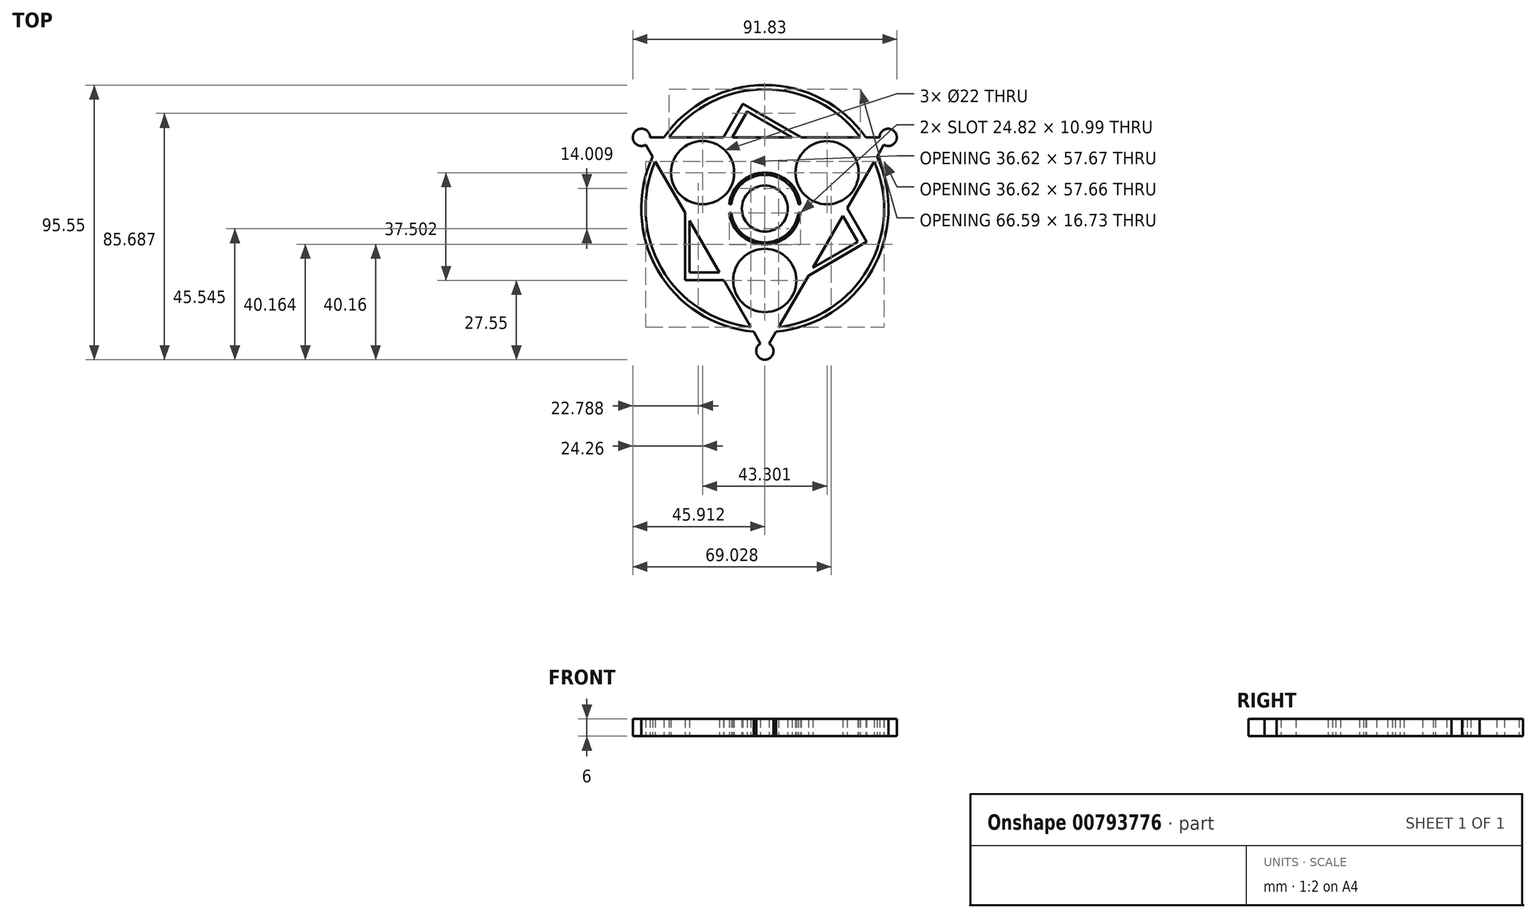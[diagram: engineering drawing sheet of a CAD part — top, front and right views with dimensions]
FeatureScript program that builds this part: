
annotation { "Feature Type Name" : "Feature", "Feature Type Description" : "" }
export const myFeature = defineFeature(function(context is Context, id is Id, definition is map)
    precondition{}
    {
        {
            var Q0;
            Q0=qCreatedBy(makeId("Top.planeOp"),FACE);
            var sketch = newSketch(context, id + "F0", { "sketchPlane" : qUnion([Q0])});
            skCircle(sketch, "E0", {"center": v(0, 0) * mm, "radius": 8 * mm});
            skLineSegment(sketch, "E1.0", {"start": v(41.42, 22.17) * mm, "end": v(39.03, 18.04) * mm});
            skLineSegment(sketch, "E1.1", {"start": v(-1.5, -46.95) * mm, "end": v(-3.89, -42.82) * mm});
            skLineSegment(sketch, "E1.2", {"start": v(-39.91, 24.78) * mm, "end": v(-35.14, 24.78) * mm});
            skPoint(sketch, "E1.0.midPoint", {"position": v(21.46, -12.39) * mm});
            skArc(sketch, "E2", {"start": v(3.88, -42.82) * mm, "mid": v(37.24, -21.5) * mm, "end": v(39.03, 18.04) * mm});
            skArc(sketch, "E3", {"start": v(4.8, -41.22) * mm, "mid": v(35.94, -20.75) * mm, "end": v(38.1, 16.44) * mm});
            skLineSegment(sketch, "E4.trimOffspring", {"start": v(3.88, -42.82) * mm, "end": v(1.5, -46.95) * mm});
            skLineSegment(sketch, "E5.trimOffspring", {"start": v(-4.81, -41.22) * mm, "end": v(-14.23, -24.9) * mm});
            skArc(sketch, "E6.trimOffspring", {"start": v(35.15, 24.77) * mm, "mid": v(0, 43) * mm, "end": v(-35.14, 24.78) * mm});
            skArc(sketch, "E7.trimOffspring", {"start": v(33.3, 24.77) * mm, "mid": v(0, 41.5) * mm, "end": v(-33.3, 24.78) * mm});
            skLineSegment(sketch, "E8.trimOffspring", {"start": v(35.15, 24.77) * mm, "end": v(39.92, 24.77) * mm});
            skLineSegment(sketch, "E9.trimOffspring", {"start": v(38.1, 16.44) * mm, "end": v(28.68, 0.12) * mm});
            skArc(sketch, "E10.trimOffspring", {"start": v(-39.03, 18.05) * mm, "mid": v(-37.24, -21.5) * mm, "end": v(-3.89, -42.82) * mm});
            skArc(sketch, "E11.trimOffspring", {"start": v(-38.1, 16.45) * mm, "mid": v(-35.94, -20.75) * mm, "end": v(-4.81, -41.22) * mm});
            skLineSegment(sketch, "E12.trimOffspring", {"start": v(-33.3, 24.78) * mm, "end": v(-14.45, 24.78) * mm});
            skLineSegment(sketch, "E13.trimOffspring", {"start": v(-39.03, 18.05) * mm, "end": v(-41.41, 22.18) * mm});
            skPoint(sketch, "E14.0.midPoint", {"position": v(-9.59, -5.4) * mm});
            skCircle(sketch, "E15", {"center": v(0, -25) * mm, "radius": 11 * mm});
            skCircle(sketch, "E16.1.0", {"center": v(21.65, 12.5) * mm, "radius": 11 * mm});
            skCircle(sketch, "E16.2.0", {"center": v(-21.65, 12.5) * mm, "radius": 11 * mm});
            skArc(sketch, "E17", {"start": v(11.65, 1.5) * mm, "mid": v(0, 11.75) * mm, "end": v(-11.65, 1.5) * mm});
            skArc(sketch, "E18", {"start": v(12.4, 1.5) * mm, "mid": v(0, 12.5) * mm, "end": v(-12.4, 1.5) * mm});
            skLineSegment(sketch, "E19", {"start": v(-12.4, 1.5) * mm, "end": v(-11.65, 1.5) * mm});
            skLineSegment(sketch, "E20.trimOffspring", {"start": v(11.65, 1.5) * mm, "end": v(12.4, 1.5) * mm});
            skArc(sketch, "E21.MirrorCS", {"start": v(11.65, -1.5) * mm, "mid": v(0, -11.75) * mm, "end": v(-11.65, -1.5) * mm});
            skArc(sketch, "E22.MirrorCS", {"start": v(12.4, -1.5) * mm, "mid": v(0, -12.5) * mm, "end": v(-12.4, -1.5) * mm});
            skArc(sketch, "E23", {"start": v(-1.5, -46.95) * mm, "mid": v(0, -52.55) * mm, "end": v(1.5, -46.95) * mm});
            skArc(sketch, "E24.1.0", {"start": v(41.42, 22.17) * mm, "mid": v(45.51, 26.27) * mm, "end": v(39.92, 24.77) * mm});
            skArc(sketch, "E24.2.0", {"start": v(-39.91, 24.78) * mm, "mid": v(-45.5, 26.28) * mm, "end": v(-41.41, 22.18) * mm});
            skLineSegment(sketch, "E25.top", {"start": v(-27.77, -24.9) * mm, "end": v(-14.23, -24.9) * mm});
            skLineSegment(sketch, "E25.left", {"start": v(-27.77, -1.44) * mm, "end": v(-27.77, -24.9) * mm});
            skLineSegment(sketch, "E26.top", {"start": v(-26.2, -22.25) * mm, "end": v(-15.77, -22.25) * mm});
            skLineSegment(sketch, "E26.left", {"start": v(-26.2, -4.17) * mm, "end": v(-26.2, -22.25) * mm});
            skLineSegment(sketch, "E27.trimOffspring", {"start": v(-27.77, -1.44) * mm, "end": v(-38.1, 16.45) * mm});
            skLineSegment(sketch, "E28.trimOffspring", {"start": v(-15.77, -22.25) * mm, "end": v(-26.2, -4.17) * mm});
            skLineSegment(sketch, "E29.1.0", {"start": v(15.14, -23.33) * mm, "end": v(35.45, -11.6) * mm});
            skLineSegment(sketch, "E29.1.1", {"start": v(35.45, -11.6) * mm, "end": v(28.68, 0.12) * mm});
            skLineSegment(sketch, "E29.1.2", {"start": v(32.37, -11.57) * mm, "end": v(27.15, -2.53) * mm});
            skLineSegment(sketch, "E29.1.3", {"start": v(16.7, -20.6) * mm, "end": v(32.37, -11.57) * mm});
            skLineSegment(sketch, "E29.1.4", {"start": v(27.15, -2.53) * mm, "end": v(16.7, -20.6) * mm});
            skLineSegment(sketch, "E29.2.0", {"start": v(12.64, 24.78) * mm, "end": v(-7.68, 36.5) * mm});
            skLineSegment(sketch, "E29.2.1", {"start": v(-7.68, 36.5) * mm, "end": v(-14.45, 24.78) * mm});
            skLineSegment(sketch, "E29.2.2", {"start": v(-6.17, 33.82) * mm, "end": v(-11.38, 24.78) * mm});
            skLineSegment(sketch, "E29.2.3", {"start": v(9.5, 24.78) * mm, "end": v(-6.17, 33.82) * mm});
            skLineSegment(sketch, "E29.2.4", {"start": v(-11.38, 24.78) * mm, "end": v(9.5, 24.78) * mm});
            skLineSegment(sketch, "E30.trimOffspring", {"start": v(15.14, -23.33) * mm, "end": v(4.8, -41.22) * mm});
            skLineSegment(sketch, "E31.trimOffspring", {"start": v(12.64, 24.78) * mm, "end": v(33.3, 24.77) * mm});
            skLineSegment(sketch, "E32.MirrorCS", {"start": v(11.65, -1.5) * mm, "end": v(12.4, -1.5) * mm});
            skLineSegment(sketch, "E33.MirrorCS", {"start": v(-12.4, -1.5) * mm, "end": v(-11.65, -1.5) * mm});
            skSolve(sketch);
        }
        {
            var Q0;
            Q0 = qSketchRegion(id + "F0", true);
            extrude(context, id + "F1", {"entities" : qUnion([Q0]), "depth" : 6 * mm, "offsetDistance" : 25 * mm});
        }
    });
